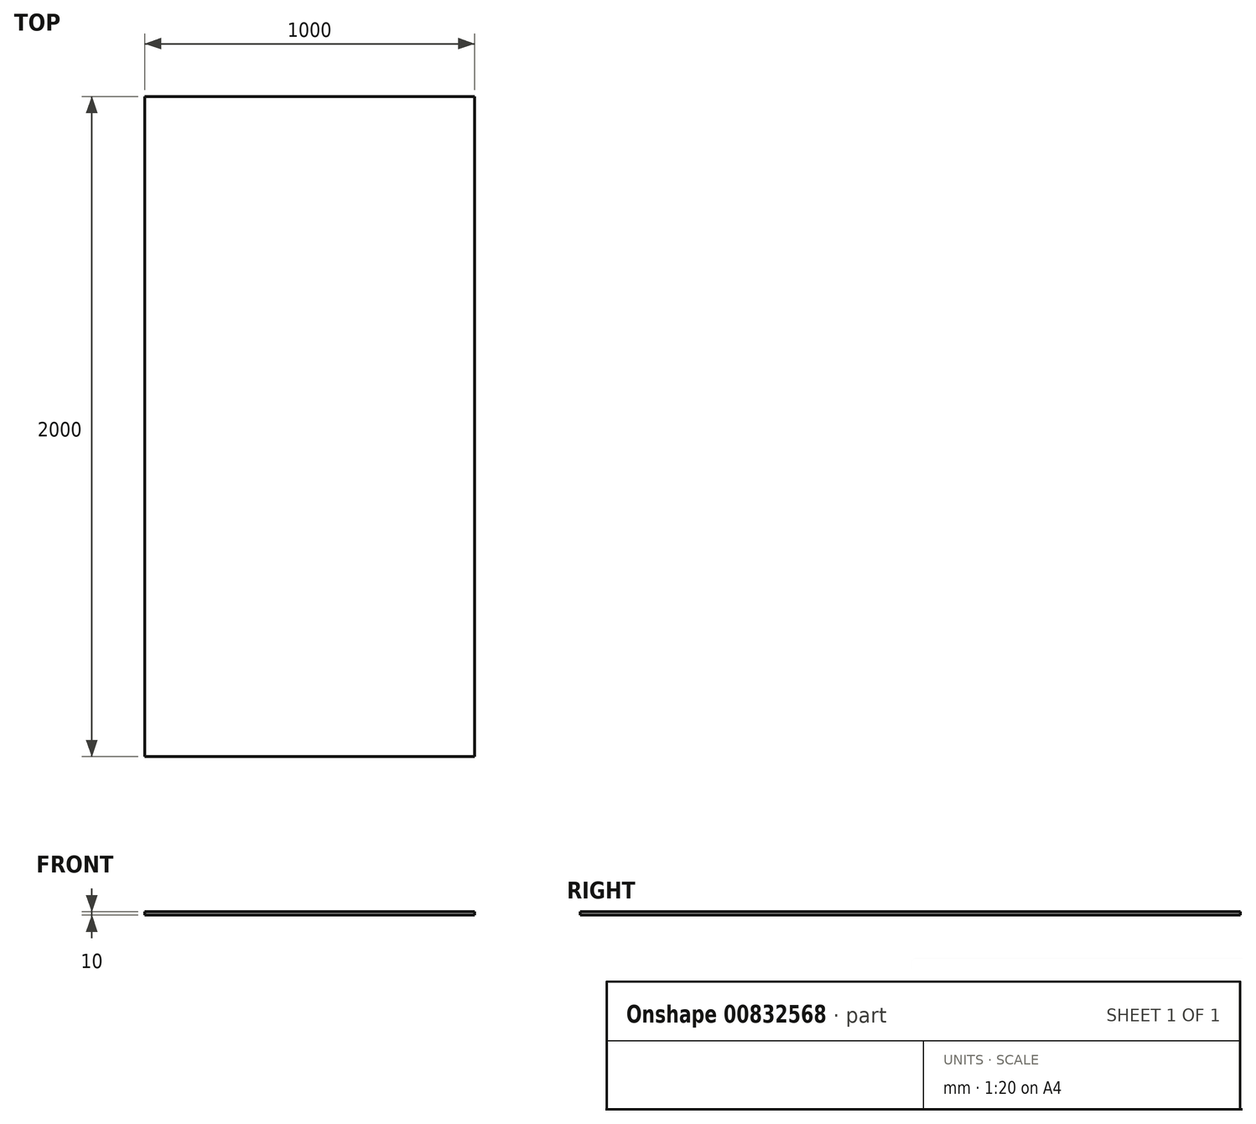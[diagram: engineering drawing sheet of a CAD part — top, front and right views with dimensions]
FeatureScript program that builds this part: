
annotation { "Feature Type Name" : "Feature", "Feature Type Description" : "" }
export const myFeature = defineFeature(function(context is Context, id is Id, definition is map)
    precondition{}
    {
        {
            var Q0;
            Q0=qCreatedBy(makeId("Top.planeOp"),FACE);
            var sketch = newSketch(context, id + "F0", { "sketchPlane" : qUnion([Q0])});
            skLineSegment(sketch, "E0.bottom", {"start": v(-500, 1000) * mm, "end": v(500, 1000) * mm});
            skLineSegment(sketch, "E0.top", {"start": v(-500, -1000) * mm, "end": v(500, -1000) * mm});
            skLineSegment(sketch, "E0.left", {"start": v(-500, 1000) * mm, "end": v(-500, -1000) * mm});
            skLineSegment(sketch, "E0.right", {"start": v(500, 1000) * mm, "end": v(500, -1000) * mm});
            skSolve(sketch);
        }
        {
            var Q0;
            Q0=makeQuery(id+"F0.imprint","IMPRINT",FACE,{"disambiguationData":[TD([[makeQuery(id+"F0.imprint","IMPRINT",EDGE,{"derivedFrom":sQuery(id+"F0.wireOp",EDGE,"E0.bottom")}),-1.0]])]});
            extrude(context, id + "F1", {"entities" : qUnion([Q0]), "depth" : 10 * mm, "offsetDistance" : 25 * mm});
        }
    });
